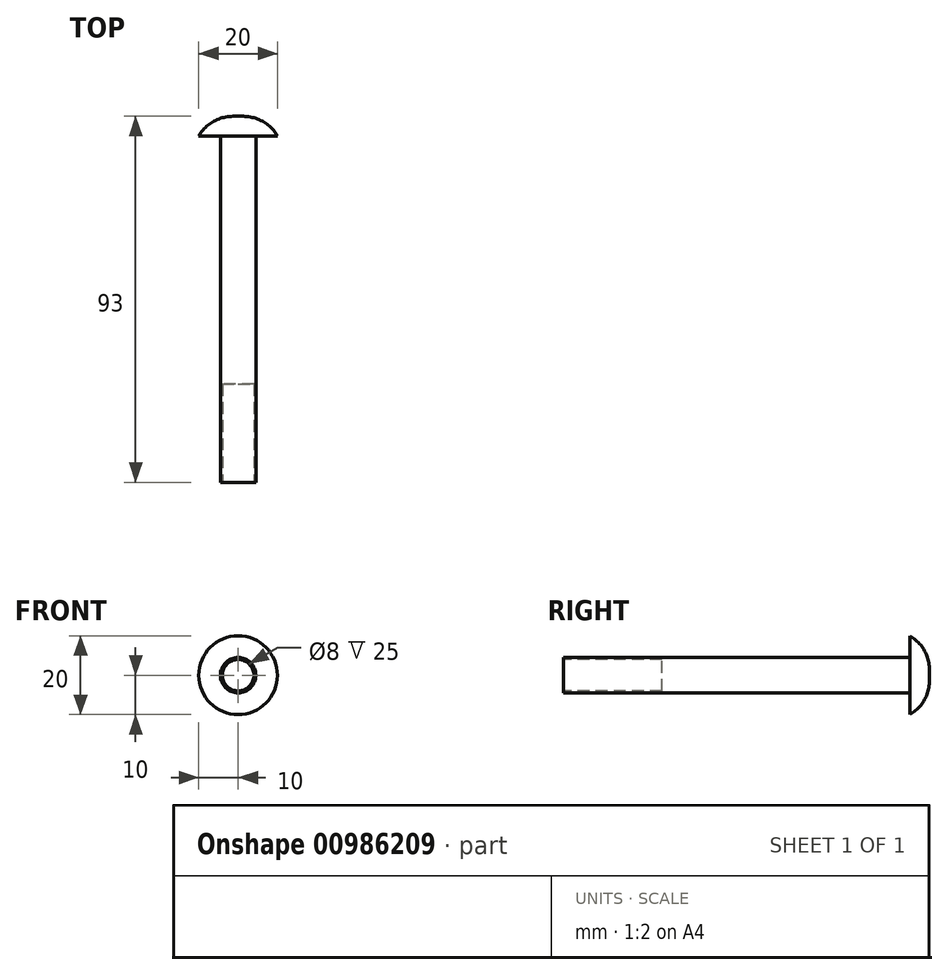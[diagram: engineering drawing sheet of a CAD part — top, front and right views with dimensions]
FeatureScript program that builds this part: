
annotation { "Feature Type Name" : "Feature", "Feature Type Description" : "" }
export const myFeature = defineFeature(function(context is Context, id is Id, definition is map)
    precondition{}
    {
        {
            var Q0;
            Q0=qCreatedBy(makeId("Front.planeOp"),FACE);
            var sketch = newSketch(context, id + "F0", { "sketchPlane" : qUnion([Q0])});
            skCircle(sketch, "E0", {"center": v(0, 0) * mm, "radius": 4.5 * mm});
            skSolve(sketch);
        }
        {
            var Q0;
            Q0 = qSketchRegion(id + "F0", true);
            extrude(context, id + "F1", {"entities" : qUnion([Q0]), "depth" : 88 * mm, "offsetDistance" : 25 * mm});
        }
        {
            var Q0;
            Q0=makeQuery(id+"F1.opExtrude","CAP_FACE",FACE,{"disambiguationData":[OSD([sQuery(id+"F0.wireOp",EDGE,"E0")])],"isStart":false});
            var sketch = newSketch(context, id + "F2", { "sketchPlane" : qUnion([Q0])});
            skCircle(sketch, "E1", {"center": v(0, 0) * mm, "radius": 4 * mm});
            skSolve(sketch);
        }
        {
            var Q0;
            Q0=makeQuery(id+"F2.imprint","IMPRINT",FACE,{"disambiguationData":[TD([[makeQuery(id+"F2.imprint","IMPRINT",EDGE,{"derivedFrom":sQuery(id+"F2.wireOp",EDGE,"E1")}),1.0]])]});
            extrude(context, id + "F3", {"entities" : qUnion([Q0]), "operationType" : NewBodyOperationType.REMOVE, "oppositeDirection" : true, "depth" : 25 * mm, "offsetDistance" : 25 * mm});
        }
        {
            var Q0;
            Q0=makeQuery(id+"F1.opExtrude","CAP_FACE",FACE,{"disambiguationData":[OSD([sQuery(id+"F0.wireOp",EDGE,"E0")])],"isStart":true});
            var sketch = newSketch(context, id + "F4", { "sketchPlane" : qUnion([Q0])});
            skCircle(sketch, "E2", {"center": v(0, 0) * mm, "radius": 10 * mm});
            skSolve(sketch);
        }
        {
            var Q0;
            Q0=makeQuery(id+"F4.imprint","IMPRINT",FACE,{"disambiguationData":[TD([[makeQuery(id+"F4.imprint","IMPRINT",EDGE,{"derivedFrom":makeQuery(id+"F1.opExtrude","CAP_EDGE",EDGE,{"disambiguationData":[OSD([sQuery(id+"F0.wireOp",EDGE,"E0")])],"isStart":true})}),-1.0]])]});
            var Q1;
            Q1=makeQuery(id+"F4.imprint","IMPRINT",FACE,{"disambiguationData":[TD([[makeQuery(id+"F4.imprint","IMPRINT",EDGE,{"derivedFrom":sQuery(id+"F4.wireOp",EDGE,"E2")}),1.0]])]});
            extrude(context, id + "F5", {"entities" : qUnion([Q0, Q1]), "operationType" : NewBodyOperationType.ADD, "depth" : 5 * mm, "offsetDistance" : 25 * mm});
        }
        {
            var Q0;
            Q0=makeQuery(id+"F5.opExtrude","CAP_EDGE",EDGE,{"disambiguationData":[OSD([sQuery(id+"F4.wireOp",EDGE,"E2")])],"isStart":false});
            fillet(context, id + "F6", {"entities" : qUnion([Q0]), "radius" : 10 * mm, "tangentPropagation" : true, "allowEdgeOverflow" : false});
        }
    });
